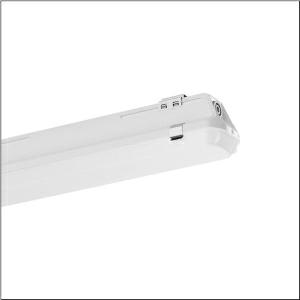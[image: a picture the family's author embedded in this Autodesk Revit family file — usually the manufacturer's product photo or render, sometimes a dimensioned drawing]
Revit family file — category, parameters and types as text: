
# Revit family: monsun_r__11_51fp107p430h_5718
name_source: partatom
category: Lighting Fixtures
units: mm (PartAtom-declared; Revit-internal decimal feet)

## family parameters
Cut with Voids When Loaded = No
Host = Face
Light Source = No
Part Type = Normal
Room Calculation Point = No
Round Connector Dimension = Use Diameter
Shared = No

## types (1)
- Monsun® 11 (1 x LED, 3970 lm, 22.2 W, 4000K)
    Apparent Load = 22 VA
    CIE Flux Codes = 47 77 93 94 100
    Color Rendering = 80
    Color Temperature = 4000K
    Default Elevation = 1800 mm
    Description = Monsun® 11, damp-proof luminaire, chain hanger, primary optical cover: enclosure, of PMMA, light emission: direct distribution, primary light characteristic: symmetric, installation type: suspended mounting, surface-mounted, horizontal mounting, vertical mounting, LED, rated luminous flux: 3.970lm, luminous efficacy: 179lm/W, light colour: 840, colour temperature: 4000K, control gear: ECG, with terminal, 3-pole, max. 2.5mm², mains connection: 220..240V, AC, 50/60Hz, rated input power: 22W, luminaire housing, of glass-fibre reinforced polyester, uncoated, bright grey, incl. chain hanger, length: 1.590mm, width: 90mm, height: 88mm, clip for enclosure, of stainless steel (V2A), ceiling mounting element, of stainless steel (V2A), chain hanger, of stainless steel (V2A), protection rating (complete): IP66, insulation class (complete): insulation class I (protective earthing), certification: CE, ENEC, VDE, UKCA, protection symbol: D, impact resistance: IK04, permissible operating ambient temperature: -35..+40°C, standard: EN 50419, EN 60598-2-1, no direct snow, no direct sun, no direct rain, for indoor or canopied outdoor use, corresponds to IFS (International Featured Standards) requirements for safety and quality in the food industry, contact your sales advisor before using the luminaires in applications with unclear chemical exposure, large temperature fluctuations or condensation-forming humidity, LABS conformity tested according to VDMA 24364:2018-05, packaging unit: 1 piece
    Height = 89 mm
    Lamp = 1 x LED
    Lamp Light Flux = 3970 lm
    Lamp Power = 22.2 W
    Lamp count = 1
    Length = 1590 mm
    Luminous efficacy = 179 lm/W
    Manufacturer = Siteco
    ModVariant = No
    Model = 51FP107P430H
    Mounting Place = Ceiling
    Mounting Type = Surface mounted
    Number of Poles = 1
    OnlyDefault = Yes
    Power Factor = 1
    Product Name = Monsun® 11
    Product group = damp-proof luminaire
    ProductGroupID = 300
    Protection Class = Protection class I
    Protection Degree = IP 66
    RLX_Detail_Level = 1
    RLX_Emergency_Light_Flux = 0 lm
    RLX_Emergency_Type = 0
    RLX_Emergency_Type_DB = No
    RlxData = <blob elided: 88569 chars, md5=4cc047ec>
    Socket = socket
    Standby Power = 0 W
    System Light Flux = 3970 lm
    System Power = 22 W
    Type Comments = Product without accessories
    Type Image = l_1004748.jpg
    URL = http://relux.com
    VarID = ---
    Voltage = 0 V
    Weight = 0.00 kg
    Width = 90 mm

## geometry (parser evidence)
native form markers: Blend x4, Sweep x13
no freeform markers — native parametric forms only
